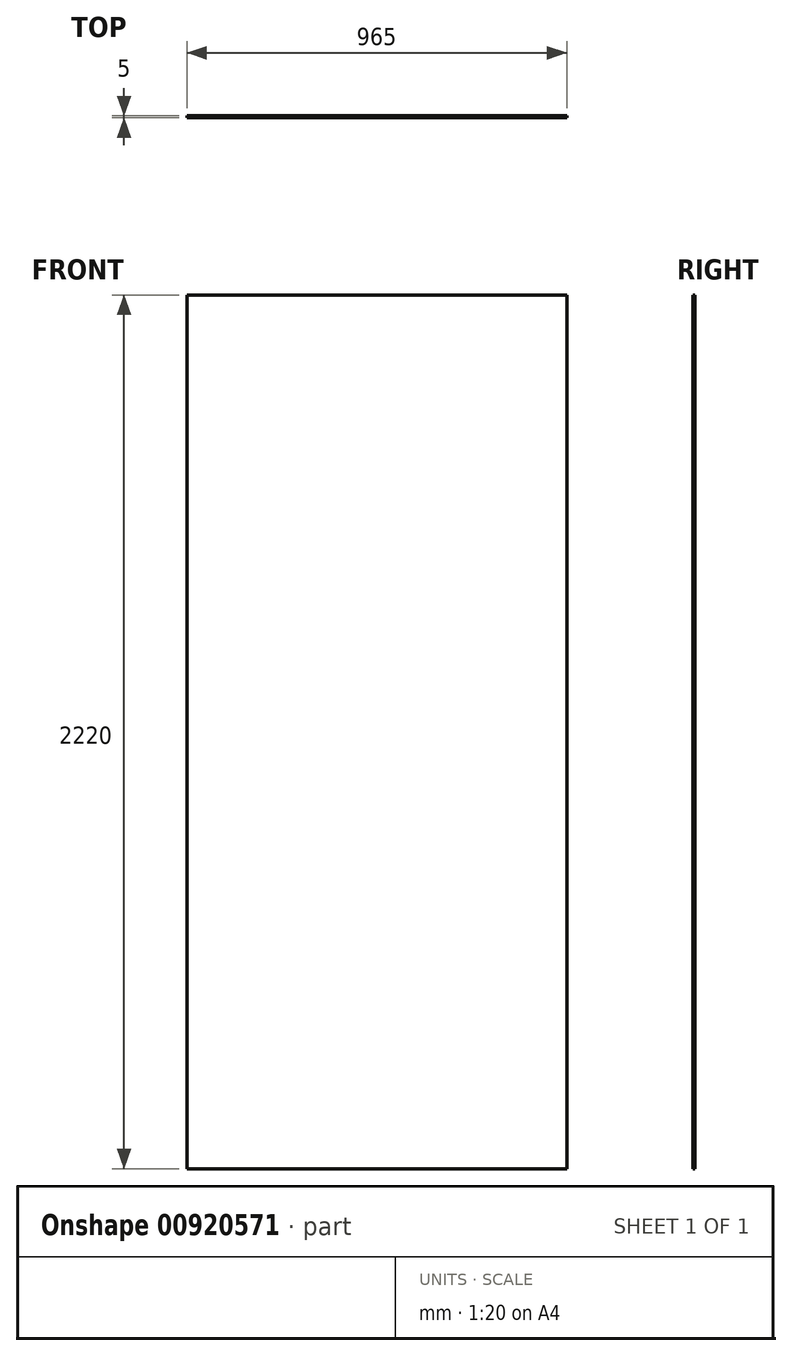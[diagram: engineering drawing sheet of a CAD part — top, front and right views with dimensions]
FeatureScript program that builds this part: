
annotation { "Feature Type Name" : "Feature", "Feature Type Description" : "" }
export const myFeature = defineFeature(function(context is Context, id is Id, definition is map)
    precondition{}
    {
        {
            var Q0;
            Q0=qCreatedBy(makeId("Front.planeOp"),FACE);
            var sketch = newSketch(context, id + "F0", { "sketchPlane" : qUnion([Q0])});
            skLineSegment(sketch, "E0.bottom", {"start": v(482.5, -1110) * mm, "end": v(-482.5, -1110) * mm});
            skLineSegment(sketch, "E0.top", {"start": v(482.5, 1110) * mm, "end": v(-482.5, 1110) * mm});
            skLineSegment(sketch, "E0.left", {"start": v(482.5, -1110) * mm, "end": v(482.5, 1110) * mm});
            skLineSegment(sketch, "E0.right", {"start": v(-482.5, -1110) * mm, "end": v(-482.5, 1110) * mm});
            skPoint(sketch, "E0.middle", {"position": v(0, 0) * mm});
            skSolve(sketch);
        }
        {
            var Q0;
            Q0 = qSketchRegion(id + "F0", true);
            extrude(context, id + "F1", {"entities" : qUnion([Q0]), "depth" : 5 * mm, "offsetDistance" : 25 * mm, "symmetric" : true});
        }
    });
